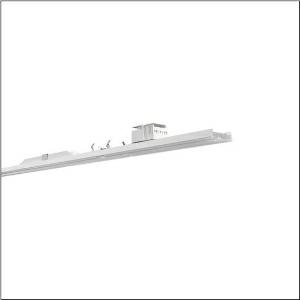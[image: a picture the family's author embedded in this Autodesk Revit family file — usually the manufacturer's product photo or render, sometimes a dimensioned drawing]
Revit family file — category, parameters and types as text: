
# Revit family: licross_r__11_recessed_ho_51tl11dn4dxrd_8a7c
name_source: partatom
category: Lighting Fixtures
units: mm (PartAtom-declared; Revit-internal decimal feet)

## family parameters
Cut with Voids When Loaded = No
Host = Face
Light Source = No
Part Type = Normal
Room Calculation Point = No
Round Connector Dimension = Use Diameter
Shared = No

## types (1)
- --- (1 x LED, 2080 lm, 13.3 W, 4000K)
    Apparent Load = 13 VA
    CIE Flux Codes = 87 95 99 100 100
    Color Rendering = 80
    Color Temperature = 4000K
    Default Elevation = 1800 mm
    Description = Licross® 11 Recessed HOluminaire insert, length: 1.500mm, width: 66mm, height: 67mm, LED rated luminous flux: 13.060lm, light colour: 840, control gear: DALI 2, control gear: ECG DALI, with plug, 6-pole, with phase selection, mains connection: 220..240V, AC/DC, 0/50..60Hz, without changeover relay, for emergency light function, for central battery installations according to DIN EN 60598-2-22, halogen-free wiring, primary optical cover: cover, of PMMA, light emission: direct distribution, protection rating (complete): IP40, insulation class (complete): insulation class I (protective earthing), certification: CE, ENEC, VDE, protection symbol: D if used in an environment without relevant dust loads with corresponding accessories, permissible ambient temperature for indoor applications: -25..+30°C, standard: EN 60598-2-22, reducing of maximum allowable ambient temperature of 5°C with ceiling mounting, corresponds to IFS (International Featured Standards) requirements for safety and quality in the food industry, packaging unit: 1 piece
    Height = 58 mm
    Lamp = 1 x LED
    Lamp Light Flux = 2080 lm
    Lamp Power = 13.3 W
    Lamp count = 1
    Length = 1500 mm
    Luminous efficacy = 156 lm/W
    Manufacturer = Siteco
    ModVariant = No
    Model = 51TL11DN4DXRD
    Mounting Place = Ceiling
    Mounting Type = Pendant
    Number of Poles = 1
    OnlyDefault = Yes
    Power Factor = 1
    Product Name = Licross® 11 Recessed HO
    Product group = luminaire insert
    ProductGroupID = 902
    Protection Class = Protection class I
    Protection Degree = IP 40
    RLX_Detail_Level = 1
    RlxData = <blob elided: 22629 chars, md5=9f3b0455>
    Socket = socket
    Standby Power = 0 W
    System Light Flux = 2080 lm
    System Power = 13 W
    Type Comments = : DC mode (central or group accumulator) initial emergency light level
    Type Image = l_1266722.jpg
    URL = http://relux.com
    VarID = @adj_134109
    Voltage = 0 V
    Weight = 0.00 kg
    Width = 66 mm

## geometry (parser evidence)
native form markers: Blend x4, Sweep x9
no freeform markers — native parametric forms only
